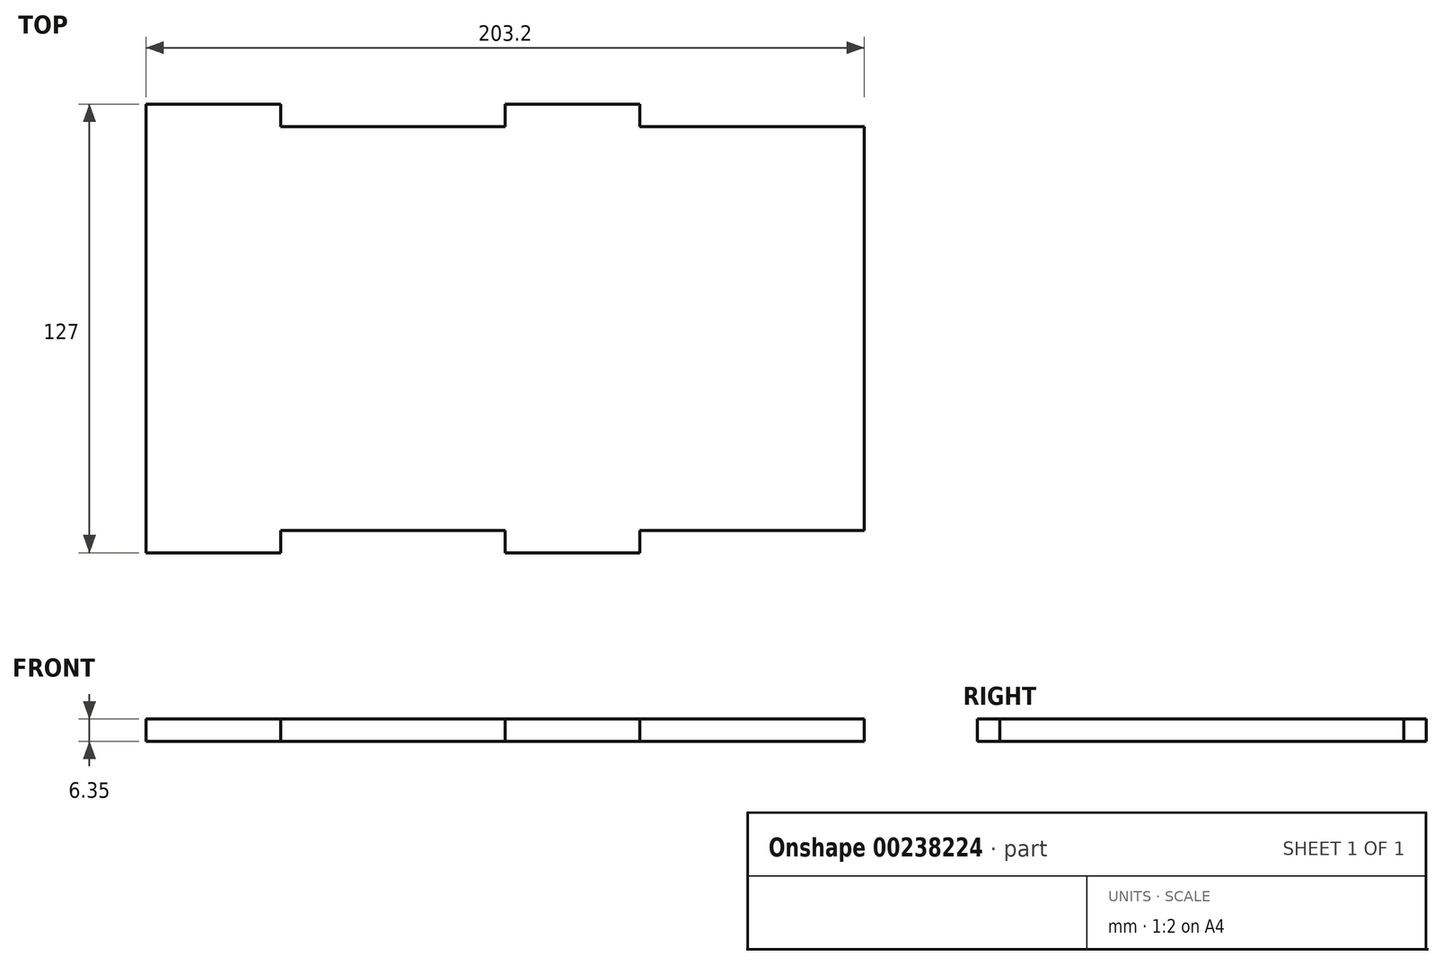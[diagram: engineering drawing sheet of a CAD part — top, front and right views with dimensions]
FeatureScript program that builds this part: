
annotation { "Feature Type Name" : "Feature", "Feature Type Description" : "" }
export const myFeature = defineFeature(function(context is Context, id is Id, definition is map)
    precondition{}
    {
        {
            var Q0;
            Q0=qCreatedBy(makeId("Top.planeOp"),FACE);
            var sketch = newSketch(context, id + "F0", { "sketchPlane" : qUnion([Q0])});
            skLineSegment(sketch, "E0.bottom", {"start": v(101.6, -63.5) * mm, "end": v(-101.6, -63.5) * mm});
            skLineSegment(sketch, "E0.top", {"start": v(101.6, 63.5) * mm, "end": v(-101.6, 63.5) * mm});
            skLineSegment(sketch, "E0.left", {"start": v(101.6, -63.5) * mm, "end": v(101.6, 63.5) * mm});
            skLineSegment(sketch, "E0.right", {"start": v(-101.6, -63.5) * mm, "end": v(-101.6, 63.5) * mm});
            skPoint(sketch, "E0.middle", {"position": v(0, 0) * mm});
            skSolve(sketch);
        }
        {
            var Q0;
            Q0=makeQuery(id+"F0.imprint","IMPRINT",FACE,{"disambiguationData":[TD([[makeQuery(id+"F0.imprint","IMPRINT",EDGE,{"derivedFrom":sQuery(id+"F0.wireOp",EDGE,"E0.bottom")}),-1.0]])]});
            extrude(context, id + "F1", {"entities" : qUnion([Q0]), "oppositeDirection" : true, "depth" : 6.35 * mm, "offsetDistance" : 25.4 * mm});
        }
        {
            var Q0;
            Q0=makeQuery(id+"F1.opExtrude","CAP_FACE",FACE,{"disambiguationData":[OSD([sQuery(id+"F0.wireOp",EDGE,"E0.bottom"),sQuery(id+"F0.wireOp",EDGE,"E0.top"),sQuery(id+"F0.wireOp",EDGE,"E0.left"),sQuery(id+"F0.wireOp",EDGE,"E0.right")])],"isStart":true});
            var sketch = newSketch(context, id + "F2", { "sketchPlane" : qUnion([Q0])});
            skLineSegment(sketch, "E1.bottom", {"start": v(101.6, 63.5) * mm, "end": v(38.1, 63.5) * mm});
            skLineSegment(sketch, "E1.top", {"start": v(101.6, 57.15) * mm, "end": v(38.1, 57.15) * mm});
            skLineSegment(sketch, "E1.left", {"start": v(101.6, 63.5) * mm, "end": v(101.6, 57.15) * mm});
            skLineSegment(sketch, "E1.right", {"start": v(38.1, 63.5) * mm, "end": v(38.1, 57.15) * mm});
            skLineSegment(sketch, "E2.bottom", {"start": v(0, 63.5) * mm, "end": v(-63.5, 63.5) * mm});
            skLineSegment(sketch, "E2.top", {"start": v(0, 57.15) * mm, "end": v(-63.5, 57.15) * mm});
            skLineSegment(sketch, "E2.left", {"start": v(0, 63.5) * mm, "end": v(0, 57.15) * mm});
            skLineSegment(sketch, "E2.right", {"start": v(-63.5, 63.5) * mm, "end": v(-63.5, 57.15) * mm});
            skLineSegment(sketch, "E3.MirrorCS", {"start": v(101.6, -57.15) * mm, "end": v(38.1, -57.15) * mm});
            skLineSegment(sketch, "E4.MirrorCS", {"start": v(101.6, -63.5) * mm, "end": v(101.6, -57.15) * mm});
            skLineSegment(sketch, "E5.MirrorCS", {"start": v(101.6, -63.5) * mm, "end": v(38.1, -63.5) * mm});
            skLineSegment(sketch, "E6.MirrorCS", {"start": v(38.1, -63.5) * mm, "end": v(38.1, -57.15) * mm});
            skLineSegment(sketch, "E7.MirrorCS", {"start": v(0, -63.5) * mm, "end": v(0, -57.15) * mm});
            skLineSegment(sketch, "E8.MirrorCS", {"start": v(0, -63.5) * mm, "end": v(-63.5, -63.5) * mm});
            skLineSegment(sketch, "E9.MirrorCS", {"start": v(0, -57.15) * mm, "end": v(-63.5, -57.15) * mm});
            skLineSegment(sketch, "E10.MirrorCS", {"start": v(-63.5, -63.5) * mm, "end": v(-63.5, -57.15) * mm});
            skSolve(sketch);
        }
        {
            var Q0;
            Q0=makeQuery(id+"F2.imprint","IMPRINT",FACE,{"disambiguationData":[TD([[makeQuery(id+"F2.imprint","IMPRINT",EDGE,{"derivedFrom":sQuery(id+"F2.wireOp",EDGE,"E2.bottom")}),1.0]])]});
            var Q1;
            Q1=makeQuery(id+"F2.imprint","IMPRINT",FACE,{"disambiguationData":[TD([[makeQuery(id+"F2.imprint","IMPRINT",EDGE,{"derivedFrom":sQuery(id+"F2.wireOp",EDGE,"E1.bottom")}),1.0]])]});
            var Q2;
            Q2=makeQuery(id+"F2.imprint","IMPRINT",FACE,{"disambiguationData":[TD([[makeQuery(id+"F2.imprint","IMPRINT",EDGE,{"derivedFrom":sQuery(id+"F2.wireOp",EDGE,"E3.MirrorCS")}),1.0]])]});
            var Q3;
            Q3=makeQuery(id+"F2.imprint","IMPRINT",FACE,{"disambiguationData":[TD([[makeQuery(id+"F2.imprint","IMPRINT",EDGE,{"derivedFrom":sQuery(id+"F2.wireOp",EDGE,"E7.MirrorCS")}),1.0]])]});
            extrude(context, id + "F3", {"entities" : qUnion([Q0, Q1, Q2, Q3]), "operationType" : NewBodyOperationType.REMOVE, "endBound" : BoundingType.UP_TO_NEXT, "oppositeDirection" : true, "depth" : 25.4 * mm, "offsetDistance" : 25.4 * mm});
        }
    });
